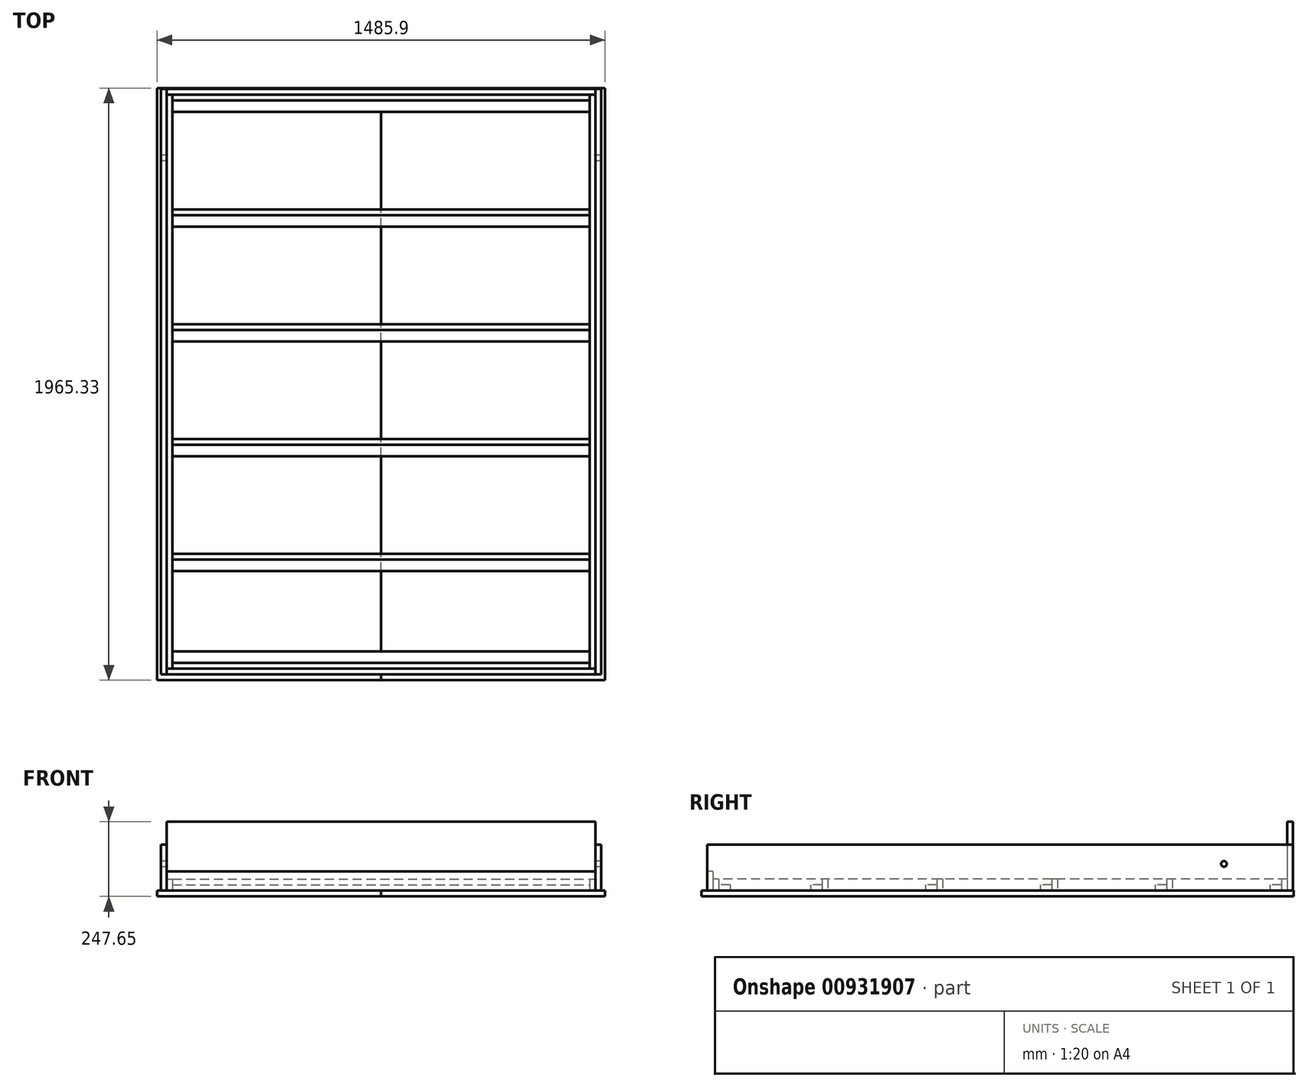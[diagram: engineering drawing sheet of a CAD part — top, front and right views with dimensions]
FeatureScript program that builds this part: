
annotation { "Feature Type Name" : "Feature", "Feature Type Description" : "" }
export const myFeature = defineFeature(function(context is Context, id is Id, definition is map)
    precondition{}
    {
        {
            var Q0;
            Q0=qCreatedBy(makeId("Top.planeOp"),FACE);
            var sketch = newSketch(context, id + "F0", { "sketchPlane" : qUnion([Q0])});
            skLineSegment(sketch, "E0.bottom", {"start": v(19.05, 0) * mm, "end": v(1403.35, 0) * mm});
            skLineSegment(sketch, "E0.top", {"start": v(19.05, -19.05) * mm, "end": v(1403.35, -19.05) * mm});
            skLineSegment(sketch, "E0.left", {"start": v(19.05, 0) * mm, "end": v(19.05, -19.05) * mm});
            skLineSegment(sketch, "E0.right", {"start": v(1403.35, 0) * mm, "end": v(1403.35, -19.05) * mm});
            skLineSegment(sketch, "E1.bottom", {"start": v(0, 0) * mm, "end": v(19.05, 0) * mm});
            skLineSegment(sketch, "E1.top", {"start": v(0, -1905) * mm, "end": v(19.05, -1905) * mm});
            skLineSegment(sketch, "E1.left", {"start": v(0, 0) * mm, "end": v(0, -1905) * mm});
            skLineSegment(sketch, "E1.right", {"start": v(19.05, 0) * mm, "end": v(19.05, -1905) * mm});
            skLineSegment(sketch, "E2.bottom", {"start": v(1403.35, 0) * mm, "end": v(1422.4, 0) * mm});
            skLineSegment(sketch, "E2.top", {"start": v(1403.35, -1905) * mm, "end": v(1422.4, -1905) * mm});
            skLineSegment(sketch, "E2.left", {"start": v(1403.35, 0) * mm, "end": v(1403.35, -1905) * mm});
            skLineSegment(sketch, "E2.right", {"start": v(1422.4, 0) * mm, "end": v(1422.4, -1905) * mm});
            skLineSegment(sketch, "E3.bottom", {"start": v(19.05, -1905) * mm, "end": v(1403.35, -1905) * mm});
            skLineSegment(sketch, "E3.top", {"start": v(19.05, -1885.95) * mm, "end": v(1403.35, -1885.95) * mm});
            skLineSegment(sketch, "E3.left", {"start": v(19.05, -1905) * mm, "end": v(19.05, -1885.95) * mm});
            skLineSegment(sketch, "E3.right", {"start": v(1403.35, -1905) * mm, "end": v(1403.35, -1885.95) * mm});
            skLineSegment(sketch, "E4", {"start": v(19.05, -1847.85) * mm, "end": v(1403.35, -1847.85) * mm});
            skLineSegment(sketch, "E5", {"start": v(19.05, -57.15) * mm, "end": v(1403.35, -57.15) * mm});
            skLineSegment(sketch, "E6.0.1.0", {"start": v(19.05, -381) * mm, "end": v(1403.35, -381) * mm});
            skLineSegment(sketch, "E6.0.1.1", {"start": v(19.05, -400.05) * mm, "end": v(1403.35, -400.05) * mm});
            skLineSegment(sketch, "E6.0.1.2", {"start": v(19.05, -438.15) * mm, "end": v(1403.35, -438.15) * mm});
            skLineSegment(sketch, "E6.0.2.0", {"start": v(19.05, -762) * mm, "end": v(1403.35, -762) * mm});
            skLineSegment(sketch, "E6.0.2.1", {"start": v(19.05, -781.05) * mm, "end": v(1403.35, -781.05) * mm});
            skLineSegment(sketch, "E6.0.2.2", {"start": v(19.05, -819.15) * mm, "end": v(1403.35, -819.15) * mm});
            skLineSegment(sketch, "E6.0.3.0", {"start": v(19.05, -1143) * mm, "end": v(1403.35, -1143) * mm});
            skLineSegment(sketch, "E6.0.3.1", {"start": v(19.05, -1162.05) * mm, "end": v(1403.35, -1162.05) * mm});
            skLineSegment(sketch, "E6.0.3.2", {"start": v(19.05, -1200.15) * mm, "end": v(1403.35, -1200.15) * mm});
            skLineSegment(sketch, "E6.0.4.0", {"start": v(19.05, -1524) * mm, "end": v(1403.35, -1524) * mm});
            skLineSegment(sketch, "E6.0.4.1", {"start": v(19.05, -1543.05) * mm, "end": v(1403.35, -1543.05) * mm});
            skLineSegment(sketch, "E6.0.4.2", {"start": v(19.05, -1581.15) * mm, "end": v(1403.35, -1581.15) * mm});
            skLineSegment(sketch, "E6.direction1", {"start": v(19.05, 0) * mm, "end": v(44.45, 0) * mm, "construction": true});
            skLineSegment(sketch, "E6.direction2", {"start": v(19.05, 0) * mm, "end": v(19.05, -381) * mm, "construction": true});
            skLineSegment(sketch, "E7", {"start": v(0, 0) * mm, "end": v(0, 19.05) * mm});
            skLineSegment(sketch, "E8", {"start": v(0, 19.05) * mm, "end": v(1422.4, 19.05) * mm});
            skLineSegment(sketch, "E9", {"start": v(1422.4, 19.05) * mm, "end": v(1422.4, 0) * mm});
            skLineSegment(sketch, "E10", {"start": v(0, -1905) * mm, "end": v(0, -1924.05) * mm});
            skLineSegment(sketch, "E11", {"start": v(0, -1924.05) * mm, "end": v(1422.4, -1924.05) * mm});
            skLineSegment(sketch, "E12", {"start": v(1422.4, -1924.05) * mm, "end": v(1422.4, -1905) * mm});
            skLineSegment(sketch, "E13", {"start": v(-19.05, 19.05) * mm, "end": v(-19.05, -1924.05) * mm});
            skLineSegment(sketch, "E14", {"start": v(-19.05, -1924.05) * mm, "end": v(0, -1924.05) * mm});
            skLineSegment(sketch, "E15", {"start": v(-19.05, 19.05) * mm, "end": v(0, 19.05) * mm});
            skLineSegment(sketch, "E16", {"start": v(1422.4, 19.05) * mm, "end": v(1441.45, 19.05) * mm});
            skLineSegment(sketch, "E17", {"start": v(1441.45, 19.05) * mm, "end": v(1441.45, -1924.05) * mm});
            skLineSegment(sketch, "E18", {"start": v(1441.45, -1924.05) * mm, "end": v(1422.4, -1924.05) * mm});
            skSolve(sketch);
        }
        {
            var Q0;
            {var subQ0=sQuery(id+"F0.wireOp",EDGE,"E0.bottom");Q0=makeQuery(id+"F0.imprint","IMPRINT",FACE,{"disambiguationData":[TD([[makeQuery(id+"F0.imprint","IMPRINT",EDGE,{"derivedFrom":subQ0}),-1.0]])]});}
            var Q1;
            {var subQ0=sQuery(id+"F0.wireOp",EDGE,"E6.0.1.0");Q1=makeQuery(id+"F0.imprint","IMPRINT",FACE,{"disambiguationData":[TD([[makeQuery(id+"F0.imprint","IMPRINT",EDGE,{"derivedFrom":subQ0}),-1.0]])]});}
            var Q2;
            {var subQ0=sQuery(id+"F0.wireOp",EDGE,"E6.0.2.0");Q2=makeQuery(id+"F0.imprint","IMPRINT",FACE,{"disambiguationData":[TD([[makeQuery(id+"F0.imprint","IMPRINT",EDGE,{"derivedFrom":subQ0}),-1.0]])]});}
            var Q3;
            {var subQ0=sQuery(id+"F0.wireOp",EDGE,"E6.0.3.0");Q3=makeQuery(id+"F0.imprint","IMPRINT",FACE,{"disambiguationData":[TD([[makeQuery(id+"F0.imprint","IMPRINT",EDGE,{"derivedFrom":subQ0}),-1.0]])]});}
            var Q4;
            {var subQ0=sQuery(id+"F0.wireOp",EDGE,"E6.0.4.0");Q4=makeQuery(id+"F0.imprint","IMPRINT",FACE,{"disambiguationData":[TD([[makeQuery(id+"F0.imprint","IMPRINT",EDGE,{"derivedFrom":subQ0}),-1.0]])]});}
            var Q5;
            Q5=makeQuery(id+"F0.imprint","IMPRINT",FACE,{"disambiguationData":[TD([[makeQuery(id+"F0.imprint","IMPRINT",EDGE,{"derivedFrom":sQuery(id+"F0.wireOp",EDGE,"E3.bottom")}),1.0]])]});
            extrude(context, id + "F1", {"entities" : qUnion([Q0, Q1, Q2, Q3, Q4, Q5]), "depth" : 38.1 * mm, "offsetDistance" : 25.4 * mm});
        }
        {
            var Q0;
            {var subQ8=sQuery(id+"F0.wireOp",EDGE,"E1.bottom");Q0=makeQuery(id+"F0.imprint","IMPRINT",FACE,{"disambiguationData":[TD([[makeQuery(id+"F0.imprint","IMPRINT",EDGE,{"derivedFrom":subQ8}),-1.0]])]});}
            var Q1;
            {var subQ8=sQuery(id+"F0.wireOp",EDGE,"E2.bottom");Q1=makeQuery(id+"F0.imprint","IMPRINT",FACE,{"disambiguationData":[TD([[makeQuery(id+"F0.imprint","IMPRINT",EDGE,{"derivedFrom":subQ8}),-1.0]])]});}
            extrude(context, id + "F2", {"entities" : qUnion([Q0, Q1]), "depth" : 38.1 * mm, "offsetDistance" : 25.4 * mm});
        }
        {
            var Q0;
            {var subQ0=sQuery(id+"F0.wireOp",EDGE,"E0.top");Q0=makeQuery(id+"F0.imprint","IMPRINT",FACE,{"disambiguationData":[TD([[makeQuery(id+"F0.imprint","IMPRINT",EDGE,{"derivedFrom":subQ0}),-1.0]])]});}
            var Q1;
            {var subQ0=sQuery(id+"F0.wireOp",EDGE,"E6.0.1.1");Q1=makeQuery(id+"F0.imprint","IMPRINT",FACE,{"disambiguationData":[TD([[makeQuery(id+"F0.imprint","IMPRINT",EDGE,{"derivedFrom":subQ0}),-1.0]])]});}
            var Q2;
            {var subQ0=sQuery(id+"F0.wireOp",EDGE,"E6.0.2.1");Q2=makeQuery(id+"F0.imprint","IMPRINT",FACE,{"disambiguationData":[TD([[makeQuery(id+"F0.imprint","IMPRINT",EDGE,{"derivedFrom":subQ0}),-1.0]])]});}
            var Q3;
            {var subQ0=sQuery(id+"F0.wireOp",EDGE,"E6.0.3.1");Q3=makeQuery(id+"F0.imprint","IMPRINT",FACE,{"disambiguationData":[TD([[makeQuery(id+"F0.imprint","IMPRINT",EDGE,{"derivedFrom":subQ0}),-1.0]])]});}
            var Q4;
            {var subQ0=sQuery(id+"F0.wireOp",EDGE,"E6.0.4.1");Q4=makeQuery(id+"F0.imprint","IMPRINT",FACE,{"disambiguationData":[TD([[makeQuery(id+"F0.imprint","IMPRINT",EDGE,{"derivedFrom":subQ0}),-1.0]])]});}
            var Q5;
            {var subQ0=sQuery(id+"F0.wireOp",EDGE,"E3.top");Q5=makeQuery(id+"F0.imprint","IMPRINT",FACE,{"disambiguationData":[TD([[makeQuery(id+"F0.imprint","IMPRINT",EDGE,{"derivedFrom":subQ0}),1.0]])]});}
            extrude(context, id + "F3", {"entities" : qUnion([Q0, Q1, Q2, Q3, Q4, Q5]), "depth" : 19.05 * mm, "offsetDistance" : 25.4 * mm});
        }
        {
            var Q0;
            Q0=makeQuery(id+"F0.imprint","IMPRINT",FACE,{"disambiguationData":[TD([[makeQuery(id+"F0.imprint","IMPRINT",EDGE,{"derivedFrom":sQuery(id+"F0.wireOp",EDGE,"E0.bottom")}),1.0]])]});
            extrude(context, id + "F4", {"entities" : qUnion([Q0]), "depth" : 228.6 * mm, "offsetDistance" : 25.4 * mm});
        }
        {
            var Q0;
            Q0=makeQuery(id+"F0.imprint","IMPRINT",FACE,{"disambiguationData":[TD([[makeQuery(id+"F0.imprint","IMPRINT",EDGE,{"derivedFrom":sQuery(id+"F0.wireOp",EDGE,"E1.top")}),-1.0]])]});
            extrude(context, id + "F5", {"entities" : qUnion([Q0]), "depth" : 63.5 * mm, "offsetDistance" : 25.4 * mm});
        }
        {
            var Q0;
            Q0=makeQuery(id+"F0.imprint","IMPRINT",FACE,{"disambiguationData":[TD([[makeQuery(id+"F0.imprint","IMPRINT",EDGE,{"derivedFrom":sQuery(id+"F0.wireOp",EDGE,"E2.right")}),1.0]])]});
            var Q1;
            Q1=makeQuery(id+"F0.imprint","IMPRINT",FACE,{"disambiguationData":[TD([[makeQuery(id+"F0.imprint","IMPRINT",EDGE,{"derivedFrom":sQuery(id+"F0.wireOp",EDGE,"E1.left")}),-1.0]])]});
            extrude(context, id + "F6", {"entities" : qUnion([Q0, Q1]), "depth" : 152.4 * mm, "offsetDistance" : 25.4 * mm});
        }
        {
            var Q0;
            Q0=qCreatedBy(makeId("Top.planeOp"),FACE);
            var sketch = newSketch(context, id + "F7", { "sketchPlane" : qUnion([Q0])});
            skLineSegment(sketch, "E19.bottom", {"start": v(-31.75, -1943.1) * mm, "end": v(1454.15, -1943.1) * mm});
            skLineSegment(sketch, "E19.top", {"start": v(-31.75, 22.22) * mm, "end": v(1454.15, 22.23) * mm});
            skLineSegment(sketch, "E19.left", {"start": v(-31.75, -1943.1) * mm, "end": v(-31.75, 22.22) * mm});
            skLineSegment(sketch, "E19.right", {"start": v(1454.15, -1943.1) * mm, "end": v(1454.15, 22.23) * mm});
            skLineSegment(sketch, "E20", {"start": v(711.2, -1943.1) * mm, "end": v(711.2, 22.23) * mm});
            skSolve(sketch);
        }
        {
            var Q0;
            {var subQ0=sQuery(id+"F7.wireOp",EDGE,"E19.left");Q0=makeQuery(id+"F7.imprint","IMPRINT",FACE,{"disambiguationData":[TD([[makeQuery(id+"F7.imprint","IMPRINT",EDGE,{"derivedFrom":subQ0}),-1.0]])]});}
            extrude(context, id + "F8", {"entities" : qUnion([Q0]), "oppositeDirection" : true, "depth" : 19.05 * mm, "offsetDistance" : 25.4 * mm});
        }
        {
            var Q0;
            {var subQ0=sQuery(id+"F7.wireOp",EDGE,"E19.right");Q0=makeQuery(id+"F7.imprint","IMPRINT",FACE,{"disambiguationData":[TD([[makeQuery(id+"F7.imprint","IMPRINT",EDGE,{"derivedFrom":subQ0}),1.0]])]});}
            extrude(context, id + "F9", {"entities" : qUnion([Q0]), "oppositeDirection" : true, "depth" : 19.05 * mm, "offsetDistance" : 25.4 * mm});
        }
        {
            var Q0;
            Q0=makeQuery(id+"F6.opExtrude","SWEPT_FACE",FACE,{"disambiguationData":[OSD([sQuery(id+"F0.wireOp",EDGE,"E2.right"),sQuery(id+"F0.wireOp",EDGE,"E9"),sQuery(id+"F0.wireOp",EDGE,"E12")])]});
            var sketch = newSketch(context, id + "F10", { "sketchPlane" : qUnion([Q0])});
            skCircle(sketch, "E21", {"center": v(209.55, 88.9) * mm, "radius": 9.53 * mm});
            skSolve(sketch);
        }
        {
            var Q0;
            Q0 = qSketchRegion(id + "F10", true);
            extrude(context, id + "F11", {"entities" : qUnion([Q0]), "operationType" : NewBodyOperationType.REMOVE, "endBound" : BoundingType.THROUGH_ALL, "oppositeDirection" : true, "depth" : 25.4 * mm, "offsetDistance" : 25.4 * mm, "hasSecondDirection" : true, "secondDirectionBound" : BoundingType.THROUGH_ALL, "secondDirectionOppositeDirection" : false, "secondDirectionDepth" : 25.4 * mm});
        }
    });
